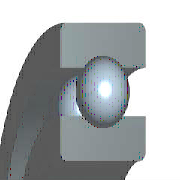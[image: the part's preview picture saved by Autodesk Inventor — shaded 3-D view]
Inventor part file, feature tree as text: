
AUTODESK INVENTOR PART (.ipt)
format: ipt  version: 2024.2 (Build 282272000, 272)  size: 333,824 bytes
history: native  units: mm (DEFAULTED — no unit token found)
features: other x6, plane x2, pattern_circular x1
ambient origin geometry x8: Origin, YZ Plane, XZ Plane, XY Plane, X Axis, Y Axis, Z Axis, Center Point
bodies: Solid1 (feature_tree)
feature tree (9):
  other  "WorkPoint1"
  other  "Drehung1"
  other  "WorkAxis1"
  plane  "WorkPlane3"
  other  "Drehung2"
  plane  "WorkPlane4"
  other  "WorkPoint2"
  other  "Drehung3"
  pattern_circular  "Polare Anordnung1"  Count=2  [1 undecoded]
note: 1 required parameter value undecoded (feature->parameter linkage not recoverable at this tier; creation-order binding heuristic only, values carry confidence <= 0.55)
